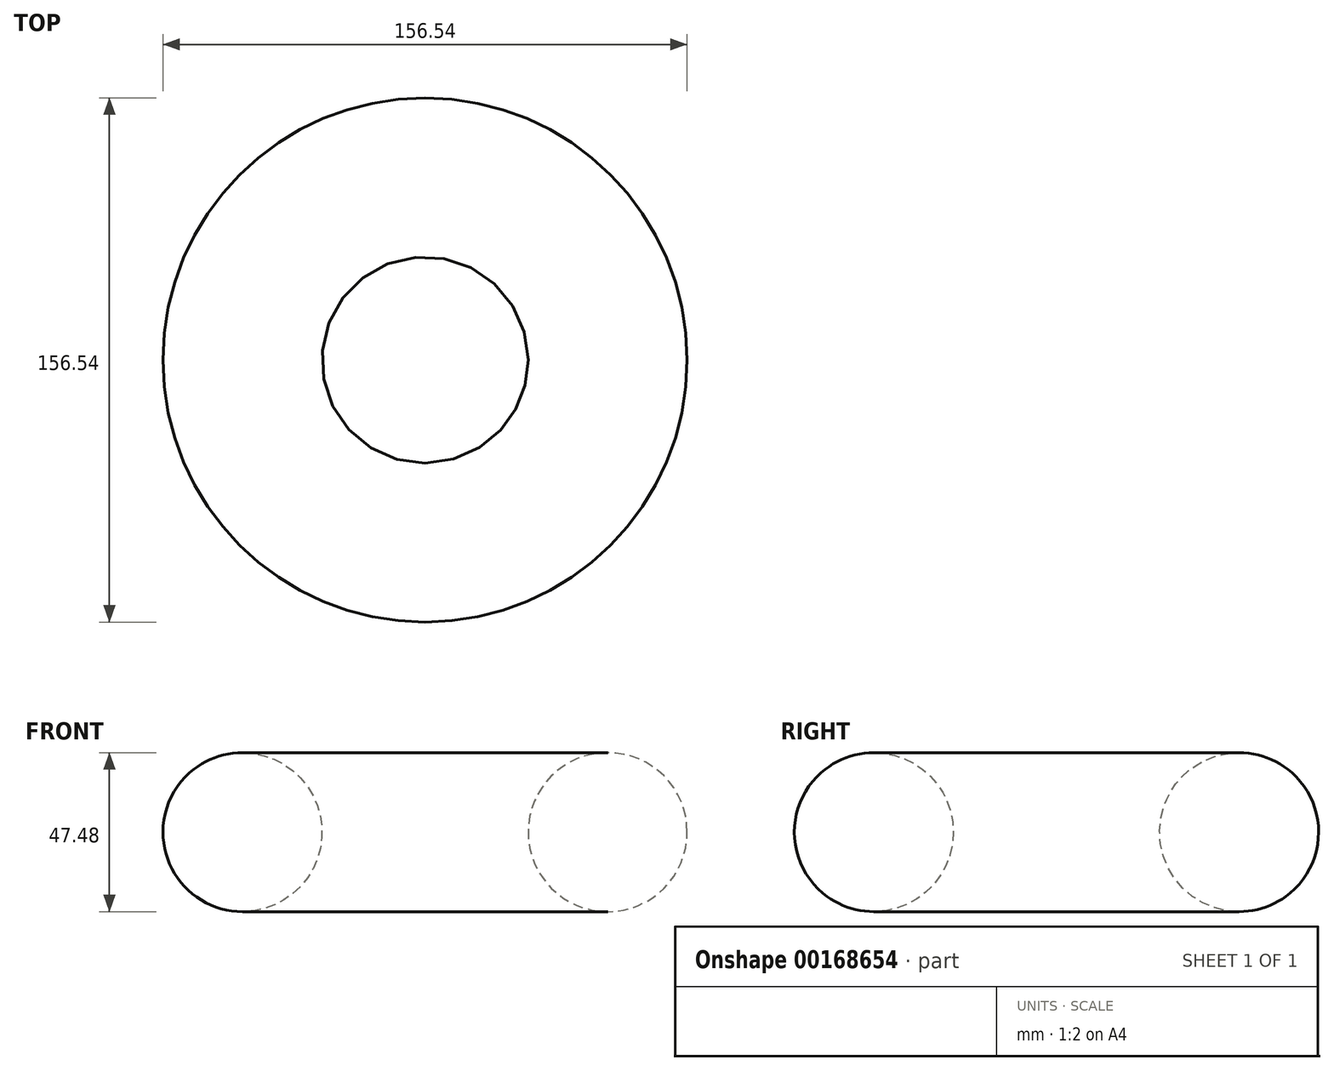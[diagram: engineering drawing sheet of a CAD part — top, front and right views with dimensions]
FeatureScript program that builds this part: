
annotation { "Feature Type Name" : "Feature", "Feature Type Description" : "" }
export const myFeature = defineFeature(function(context is Context, id is Id, definition is map)
    precondition{}
    {
        {
            var Q0;
            Q0=qCreatedBy(makeId("Front.planeOp"),FACE);
            var sketch = newSketch(context, id + "F0", { "sketchPlane" : qUnion([Q0])});
            skCircle(sketch, "E0", {"center": v(-46.93, 0) * mm, "radius": 23.74 * mm});
            skSolve(sketch);
        }
        {
            var Q0;
            Q0=qCreatedBy(makeId("Front.planeOp"),FACE);
            var sketch = newSketch(context, id + "F1", { "sketchPlane" : qUnion([Q0])});
            skLineSegment(sketch, "E1", {"start": v(7.6, 51.1) * mm, "end": v(7.6, -55.87) * mm, "construction": true});
            skSolve(sketch);
        }
        {
            var Q0;
            Q0=makeQuery(id+"F0.imprint","IMPRINT",FACE,{"disambiguationData":[TD([[makeQuery(id+"F0.imprint","IMPRINT",EDGE,{"derivedFrom":sQuery(id+"F0.wireOp",EDGE,"E0")}),1.0]])]});
            var Q1;
            Q1=sQuery(id+"F1.wireOp",EDGE,"E1");
            revolve(context, id + "F2", {"entities" : qUnion([Q0]), "axis" : qUnion([Q1]), "revolveType" : RevolveType.FULL});
        }
    });
